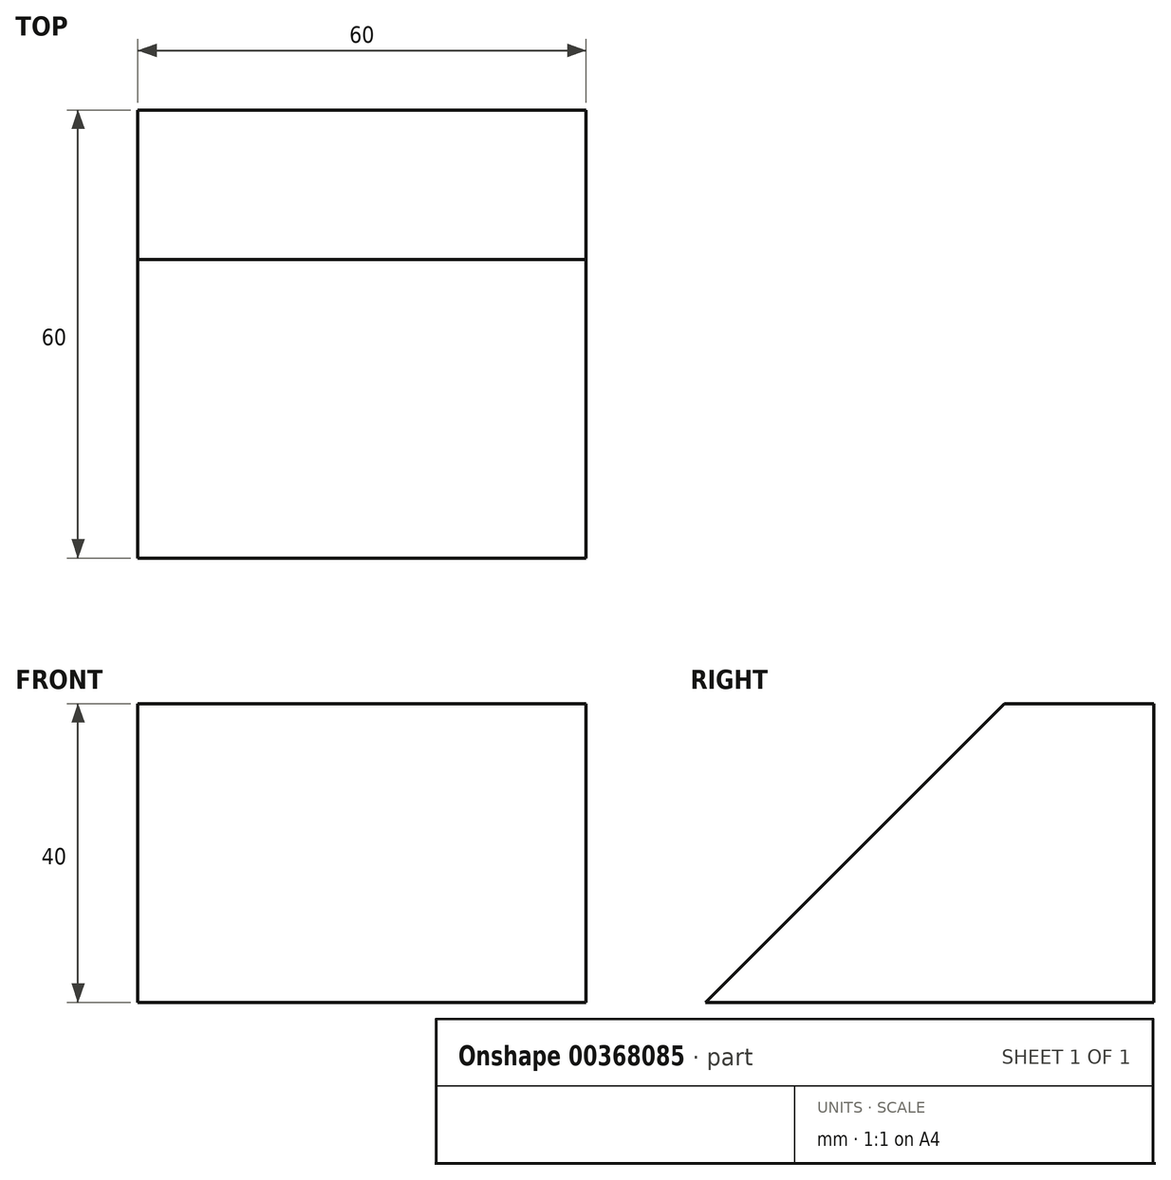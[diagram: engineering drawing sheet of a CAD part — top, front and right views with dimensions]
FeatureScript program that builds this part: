
annotation { "Feature Type Name" : "Feature", "Feature Type Description" : "" }
export const myFeature = defineFeature(function(context is Context, id is Id, definition is map)
    precondition{}
    {
        {
            var Q0;
            Q0=qCreatedBy(makeId("Right.planeOp"),FACE);
            var sketch = newSketch(context, id + "F0", { "sketchPlane" : qUnion([Q0])});
            skLineSegment(sketch, "E0", {"start": v(0, 0) * mm, "end": v(0, 40) * mm});
            skLineSegment(sketch, "E1", {"start": v(0, 40) * mm, "end": v(-20, 40) * mm});
            skLineSegment(sketch, "E2", {"start": v(-20, 40) * mm, "end": v(-60, 0) * mm});
            skLineSegment(sketch, "E3", {"start": v(-60, 0) * mm, "end": v(0, 0) * mm});
            skPoint(sketch, "E4", {"position": v(-40, 30) * mm});
            skSolve(sketch);
        }
        {
            var Q0;
            Q0=makeQuery(id+"F0.imprint","IMPRINT",FACE,{"disambiguationData":[TD([[makeQuery(id+"F0.imprint","IMPRINT",EDGE,{"derivedFrom":sQuery(id+"F0.wireOp",EDGE,"E0")}),1.0]])]});
            extrude(context, id + "F1", {"entities" : qUnion([Q0]), "depth" : 60 * mm});
        }
        {
            var Q1;
            Q1=qCreatedBy(makeId("Origin.pointOp"),VERTEX);
            var Q2;
            Q2=makeQuery(id+"F1.opExtrude","SWEPT_FACE",FACE,{"disambiguationData":[OSD([sQuery(id+"F0.wireOp",EDGE,"E2")])]});
            loft(context, id + "F2", {"operationType" : NewBodyOperationType.ADD, "sheetProfilesArray" : [{ "sheetProfileEntities" : qUnion([Q1]) }, { "sheetProfileEntities" : qUnion([Q2]) }]});
        }
    });
